# Revit family: Connected_Backflow_w-Wireless_Monitor_Zurn_Wilkins-Model_375ASTW1_(2.5-10_Inch)
name_source: partatom
category: Pipe Accessories
units: mm (PartAtom-declared; Revit-internal decimal feet)

## family parameters
Always vertical = Yes
Cut with Voids When Loaded = No
OmniClass Number = 23.65.55.14.21
OmniClass Title = Non-Return Valves for Liquid Services
Part Type = Breaks Into
Round Connector Dimension = Use Radius
Shared = No
Work Plane-Based = No

## types (6) — shared parameters
Assembly Code = D2020300
Default Elevation = 0' - 0"
Description = Reduced Pressure Principle Assembly with Integral Relief Valve Monitor
Edition number = 1
Flow Rate (GPM) = 0 GPM
Hydrostatic Test Pressure = 350.00 psi
Main Material = Paint - Zurn - Stainless Steel
Manufacturer = Zurn Water, LLC
Manufacturer Brand = Zurn Wilkins
Max Working Water Pressure = 175.00 psi
Max Working Water Temperature = 140 °F
Model = 375ASTW1
Modified Data = 07/10/2025
Product Documentation Link = https://files.zurn.com
Product Installation Sheet URL = https://files.zurn.com
Product Page URL = https://www.zurn.com
Product data URL = https://bimobject.com
Repair Parts URL = https://www.zurn.com
URL = https://www.zurn.com

## per-type parameters (varying)
| type | DIM A - Length | DIM B Main Body Length | DIM C Valve end | DIM D Valve End | DIM E Valve top | DIM F Relief valve end | DIM G Relief valve | Endpoint_Box_Version | First Gate Valve | Length | Main Body | Nominal Diameter | Nominal Radius | Pressure Loss at Rated Flow | Product Weight (lbs) | Rated Flow | Second Gate Valve |
| 6-375ASTW1 (6" 375ASTW1) | 3' - 7 1/2" | 1' - 10 1/4" | 0' - 5 1/2" | 0' - 10" | 2' - 6 1/2" | 0' - 10 3/4" | 0' - 11 1/4" | BF_Endpoint_Box-Valve_Mounted : 6-375AST | Gate Valve_350 A with 2 Test Cock : 6" | 3' - 7 1/2" | Main Body_375AST : 6" | 0' - 6" | 0' - 3" | 9.80 psi | 291 | 1000 GPM | Gate Valve_350 A with 1 Test Cock : 6" |
| 4-375ASTW1 (4" 375ASTW1) | 2' - 10 7/8" | 1' - 4 5/8" | 0' - 4 1/2" | 0' - 8 1/2" | 2' - 2 1/2" | 0' - 9 3/4" | 0' - 8 5/8" | BF_Endpoint_Box-Valve_Mounted : 4-375AST | Gate Valve_350 A with 2 Test Cock : 4" | 2' - 10 7/8" | Main Body_375AST : 4" | 0' - 4" | 0' - 2" | 11.00 psi | 179 | 500 GPM | Gate Valve_350 A with 1 Test Cock : 4" |
| 3-375ASTW1 (3" 375ASTW1) | 2' - 8 7/8" | 1' - 4 5/8" | 0' - 4 1/2" | 0' - 8 1/2" | 2' - 2 5/16" | 0' - 9 3/4" | 0' - 8 5/8" | BF_Endpoint_Box-Valve_Mounted : 3-375AST | Gate Valve_350 A with 2 Test Cock : 3" | 2' - 8 7/8" | Main Body_375AST : 3" | 0' - 3" | 0' - 1 1/2" | 11.00 psi | 122 | 320 GPM | Gate Valve_350 A with 1 Test Cock : 3" |
| 212-375ASTW1 (2 1/2" 375ASTW1) | 2' - 7 7/8" | 1' - 4 5/8" | 0' - 4 1/2" | 0' - 8 1/2" | 2' - 2 1/8" | 0' - 9 3/4" | 0' - 8 5/8" | BF_Endpoint_Box-Valve_Mounted : 212-375AST | Gate Valve_350 A with 2 Test Cock : 2 1/2" | 2' - 7 7/8" | Main Body_375AST : 2 1/2" | 0' - 2 1/2" | 0' - 1 1/4" | 9.50 psi | 105 | 220 GPM | Gate Valve_350 A with 1 Test Cock : 2 1/2" |
| 8-375ASTW1 (8" 375ASTW1) | 4' - 4 3/4" | 2' - 5 1/2" | 0' - 9 1/4" | 0' - 11" | 2' - 10 1/2" | 1' - 3 5/8" | 1' - 1 1/4" | BF_Endpoint_Box-Valve_Mounted : 8-375AST | Gate Valve_350 A with 2 Test Cock : 8" | 2' - 10 7/8" | Main Body_375AST : 8" | 0' - 8" | 0' - 4" | 10.20 psi | 579 | 1600 GPM | Gate Valve_350 A with 1 Test Cock : 8" |
| 10-375ASTW1 (10" 375ASTW1) | 4' - 7 3/4" | 4' - 1 3/4" | 0' - 9 1/4" | 1' - 0" | 2' - 10 1/2" | 1' - 3 5/8" | 1' - 1 1/2" | BF_Endpoint_Box-Valve_Mounted : 10-375AST | Gate Valve_350 A with 2 Test Cock : 10" | 2' - 10 7/8" | Main Body_375AST : 10" | 0' - 10" | 0' - 5" | 11.50 psi | 784 | 2300 GPM | Gate Valve_350 A with 1 Test Cock : 10" |

## geometry (parser evidence)
native form markers: Sweep x13
no freeform markers — native parametric forms only
